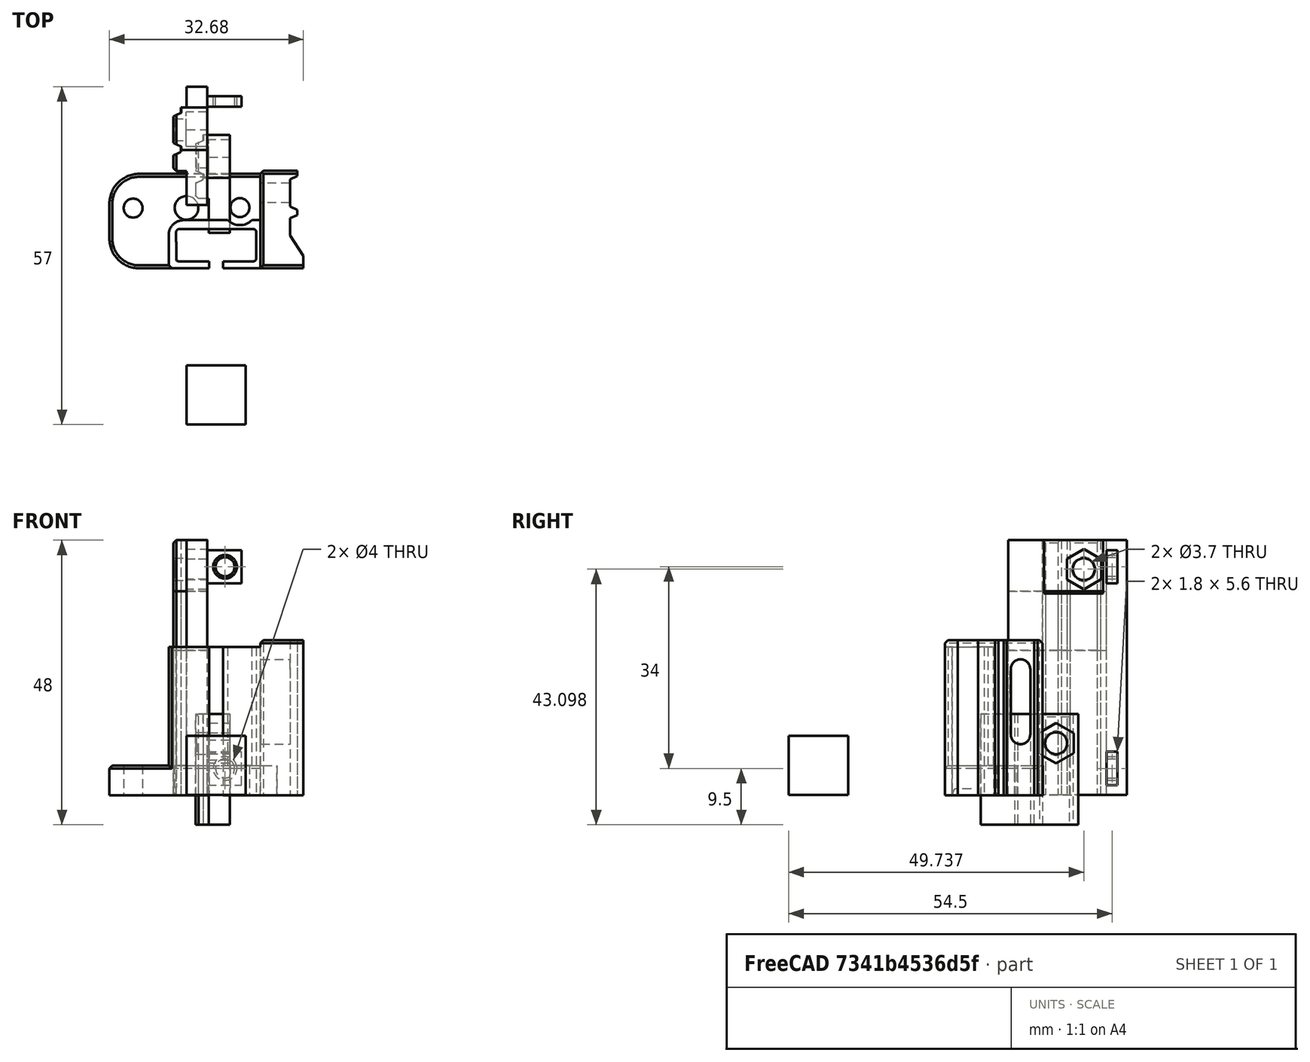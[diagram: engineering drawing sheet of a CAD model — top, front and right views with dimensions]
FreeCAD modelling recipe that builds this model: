
FCSTD DOCUMENT  (FreeCAD 0.18R14555 (Git shallow))
Label: Hemera-probe-mount
License: All rights reserved
LicenseURL: http://en.wikipedia.org/wiki/All_rights_reserved
objects: Part::Feature×14, Part::Box×8, Part::MultiCommon×3, Part::MultiFuse×3, Part::Cut×2, Part::Cylinder×2, Mesh::Feature×1, Part::Chamfer×1
note: 33 computed .brp shape members not serialized (recipe doc carries the construction recipe); baked Part::Feature solids carry a one-line shape summary decoded from their .brp

FEATURE [Part::Feature] Part__Feature  label="Part_3204332"
  Placement = pos=(-114,22,17) rot=(0,0,1;0rad)
  shape: bbox 5.737 x 34.39 x 36.52 mm, 204 faces (baked)
FEATURE [Part::Feature] Part__Feature001  label="Part_3234859"
  Placement = pos=(-98,16,19) rot=(0,0,1;0rad)
  shape: bbox 32.69 x 16.49 x 26.5 mm, 79 faces (baked)
FEATURE [Part::Feature] Part__Feature002  label="1"
  shape: bbox 2e-07 x 10.45 x 10.45 mm, 0 faces, 0 solids (baked)
FEATURE [Part::Box] Box  label="Cube"
  AttacherType = Attacher::AttachEngine3D
  Height = 10
  Length = 10
  Placement = pos=(0,-1.66,-5) rot=(0,0,1;0rad)
  Width = 9.91
  expr: Width = 15 - 5.09
FEATURE [Part::Feature] Part__Feature003  label="Part_3234860"
  Placement = pos=(-114,22,17) rot=(0,0,1;0rad)
  shape: bbox 5.737 x 34.39 x 36.52 mm, 204 faces (baked)
FEATURE [Part::MultiCommon] Common
  Placement = pos=(0,0,8.65) rot=(0,0,1;0rad)
  Shapes = -> [Box,Part__Feature003]
FEATURE [Part::Box] Box001  label="Cube001"
  AttacherType = Attacher::AttachEngine3D
  Height = 20
  Length = 17
  Placement = pos=(0,-1.66,-5) rot=(0,0,1;0rad)
  Width = 17
FEATURE [Part::MultiFuse] Fusion
  Shapes = -> [Common,Part__Feature]
FEATURE [Part::MultiCommon] Common001
  Shapes = -> [Box001,Fusion]
FEATURE [Part::Feature] Common001001  label="Common002"
  Placement = pos=(-3.78,4.66,29.35) rot=(0,0,1;0rad)
  shape: bbox 5.737 x 16.57 x 18.66 mm, 37 faces (baked)
FEATURE [Part::Box] Box002  label="Cube002"
  AttacherType = Attacher::AttachEngine3D
  Height = 5.6
  Length = 5.8
  Placement = pos=(3.5,19.6,35.7) rot=(0,0,1;0rad)
  Width = 1.8
FEATURE [Part::Box] Box003  label="Cube003"
  AttacherType = Attacher::AttachEngine3D
  Height = 43
  Length = 3.5
  Placement = pos=(0,3,0) rot=(0,0,1;0rad)
  Width = 20
FEATURE [Part::Box] Box004  label="Cube004"
  AttacherType = Attacher::AttachEngine3D
  Height = 5.6
  Length = 5.8
  Placement = pos=(3.5,19.6,1.7) rot=(0,0,1;0rad)
  Width = 1.8
FEATURE [Part::Feature] Common001002  label="Common003"
  Placement = pos=(-3.78,4.66,29.35) rot=(0,0,1;0rad)
  shape: bbox 5.737 x 16.57 x 18.66 mm, 37 faces (baked)
FEATURE [Part::Box] Box005  label="Cube005"
  AttacherType = Attacher::AttachEngine3D
  Height = 10
  Length = 10
  Placement = pos=(-2.9,0,24.4) rot=(0,0,1;0rad)
  Width = 23
FEATURE [Part::MultiCommon] Common001003
  Shapes = -> [Box005,Common001002]
FEATURE [Part::Feature] Common001003001  label="Common001004"
  shape: bbox 5.737 x 16.49 x 10 mm, 15 faces (baked)
FEATURE [Part::Feature] Common001003002  label="Common001005"
  Placement = pos=(0,0,-9.4) rot=(0,0,1;0rad)
  shape: bbox 5.737 x 16.49 x 10 mm, 15 faces (baked)
FEATURE [Part::Feature] Common001003003  label="Common001006"
  Placement = pos=(0,0,-18.8) rot=(0,0,1;0rad)
  shape: bbox 5.737 x 16.49 x 10 mm, 15 faces (baked)
FEATURE [Part::Feature] Common001003004  label="Common001007"
  Placement = pos=(0,0,-24.4) rot=(0,0,1;0rad)
  shape: bbox 5.737 x 16.49 x 10 mm, 15 faces (baked)
FEATURE [Part::Box] Box006  label="Cube006"
  AttacherType = Attacher::AttachEngine3D
  Height = 10
  Length = 10
  Placement = pos=(0,9,34) rot=(0,0,1;0rad)
  Width = 10
FEATURE [Part::Cut] Cut
  Base = -> Box003
  Tool = -> Box006
FEATURE [Part::MultiFuse] Fusion001
  Shapes = -> [Common001001,Box002,Box004,Common001003001,Common001003003,Common001003002,Common001003004,Cut]
FEATURE [Part::Cylinder] Cylinder
  Angle = 360
  AttacherType = Attacher::AttachEngine3D
  Height = 10
  Placement = pos=(6.5,17,4.5) rot=(1,0,0;4.71239rad)
  Radius = 1.6
FEATURE [Part::Cylinder] Cylinder001
  Angle = 360
  AttacherType = Attacher::AttachEngine3D
  Height = 10
  Placement = pos=(6.5,17,38.5) rot=(-1,0,0;1.5708rad)
  Radius = 1.6
FEATURE [Part::Feature] Chamfer001
  shape: bbox 11.54 x 20 x 43.01 mm, 58 faces (baked)
FEATURE [Part::Box] Box007  label="Cube007"
  AttacherType = Attacher::AttachEngine3D
  Height = 10
  Length = 10
  Placement = pos=(0,-34,0) rot=(0,0,1;0rad)
  Width = 10
FEATURE [Mesh::Feature] pinda2
FEATURE [Part::Feature] pinda2001
  shape: bbox 23.24 x 16.46 x 45 mm, 680 faces, 0 solids (baked)
FEATURE [Part::Feature] pinda2001001  label="pinda2002"
  Placement = pos=(-3.56,-7.66,0) rot=(0,0,1;0rad)
  shape: bbox 23.24 x 16.46 x 45 mm, 287 faces, 0 solids (baked)
FEATURE [Part::MultiFuse] Fusion002
  Shapes = -> [Cylinder001,Cylinder]
FEATURE [Part::Cut] Cut001
  Base = -> Fusion001
  Tool = -> Fusion002
FEATURE [Part::Chamfer] Chamfer
  Base = -> Cut001
  Edges = 1 edges r=0.5: [Edge134]
FEATURE [Part::Feature] Chamfer002
  shape: bbox 11.54 x 20 x 43.01 mm, 58 faces (baked)
